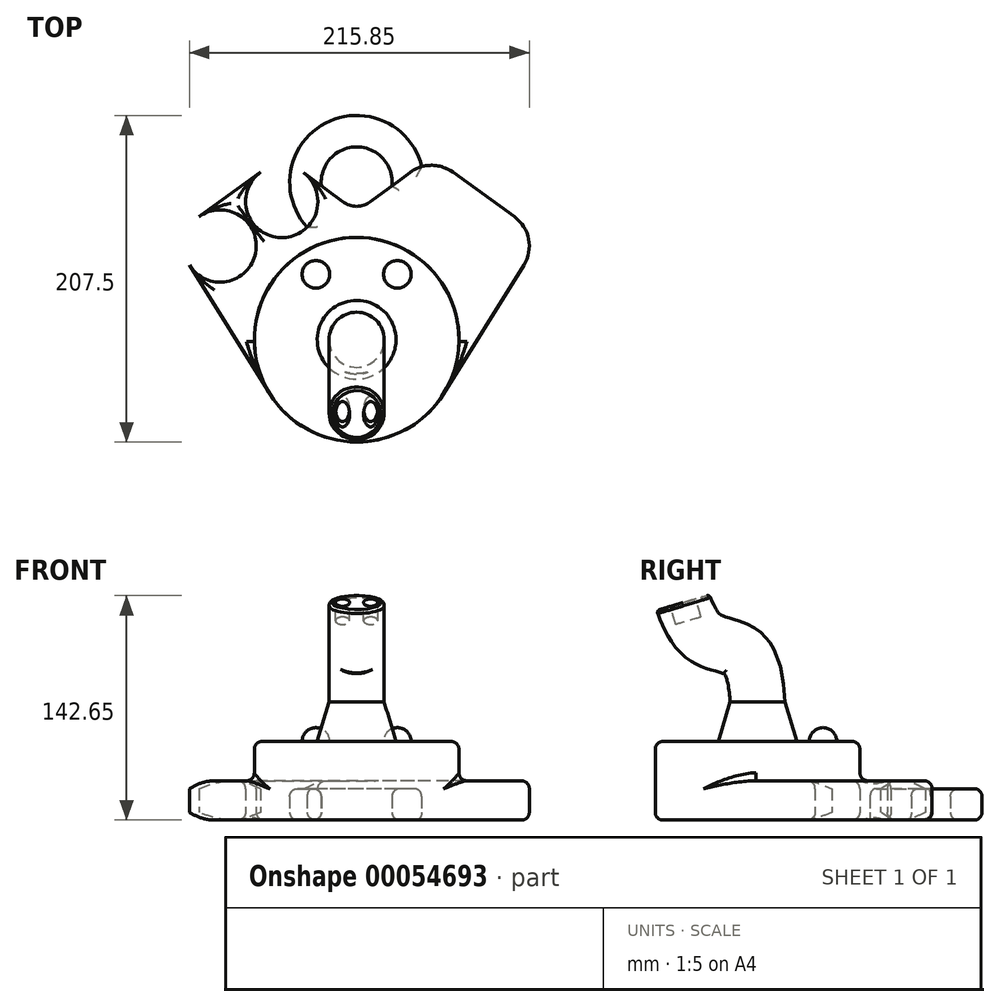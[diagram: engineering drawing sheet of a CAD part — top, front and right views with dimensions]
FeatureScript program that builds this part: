
annotation { "Feature Type Name" : "Feature", "Feature Type Description" : "" }
export const myFeature = defineFeature(function(context is Context, id is Id, definition is map)
    precondition{}
    {
        {
            var Q0;
            Q0=qCreatedBy(makeId("Top.planeOp"),FACE);
            var sketch = newSketch(context, id + "F0", { "sketchPlane" : qUnion([Q0])});
            skCircle(sketch, "E0", {"center": v(0, 0) * mm, "radius": 65 * mm});
            skSolve(sketch);
        }
        {
            var Q0;
            Q0=makeQuery(id+"F0.imprint","IMPRINT",FACE,{"disambiguationData":[TD([[makeQuery(id+"F0.imprint","IMPRINT",EDGE,{"derivedFrom":sQuery(id+"F0.wireOp",EDGE,"E0")}),1.0]])]});
            extrude(context, id + "F1", {"entities" : qUnion([Q0]), "depth" : 50 * mm});
        }
        {
            var Q0;
            Q0=makeQuery(id+"F1.opExtrude","CAP_EDGE",EDGE,{"disambiguationData":[OSD([sQuery(id+"F0.wireOp",EDGE,"E0")])],"isStart":false});
            fillet(context, id + "F2", {"entities" : qUnion([Q0]), "radius" : 5 * mm, "tangentPropagation" : true, "allowEdgeOverflow" : false});
        }
        {
            var Q0;
            Q0=makeQuery(id+"F1.opExtrude","CAP_FACE",FACE,{"disambiguationData":[OSD([sQuery(id+"F0.wireOp",EDGE,"E0")])],"isStart":false});
            var sketch = newSketch(context, id + "F3", { "sketchPlane" : qUnion([Q0])});
            skCircle(sketch, "E1", {"center": v(0, 0) * mm, "radius": 25 * mm});
            skSolve(sketch);
        }
        {
            var Q0;
            Q0=qCreatedBy(makeId("Right.planeOp"),FACE);
            var sketch = newSketch(context, id + "F4", { "sketchPlane" : qUnion([Q0])});
            skLineSegment(sketch, "E2.0", {"start": v(-25, 50) * mm, "end": v(25, 50) * mm});
            skPoint(sketch, "E3", {"position": v(0, 50) * mm});
            skLineSegment(sketch, "E4", {"start": v(0, 50) * mm, "end": v(0, 75) * mm, "construction": true});
            skSolve(sketch);
        }
        {
            var Q0;
            Q0=qCreatedBy(makeId("Top.planeOp"),FACE);
            var sketch = newSketch(context, id + "F5", { "sketchPlane" : qUnion([Q0])});
            skCircle(sketch, "E5", {"center": v(47.58, 87.83) * mm, "radius": 22.96 * mm});
            skCircle(sketch, "E6", {"center": v(86.7, 59.5) * mm, "radius": 22.96 * mm});
            skCircle(sketch, "E7.0", {"center": v(0, 0) * mm, "radius": 65 * mm});
            skLineSegment(sketch, "E8", {"start": v(106.18, 47.35) * mm, "end": v(55.14, -34.42) * mm});
            skLineSegment(sketch, "E9", {"start": v(33.87, 106.25) * mm, "end": v(-38.81, 52.14) * mm});
            skLineSegment(sketch, "E10", {"start": v(100.17, 78.1) * mm, "end": v(61.05, 106.43) * mm});
            skLineSegment(sketch, "E11", {"start": v(0, 36.31) * mm, "end": v(0, -43.27) * mm, "construction": true});
            skLineSegment(sketch, "E12.MirrorCS", {"start": v(-33.87, 106.25) * mm, "end": v(38.81, 52.14) * mm});
            skCircle(sketch, "E13.MirrorC", {"center": v(-47.58, 87.83) * mm, "radius": 22.96 * mm});
            skLineSegment(sketch, "E14.MirrorCS", {"start": v(-106.18, 47.35) * mm, "end": v(-55.14, -34.42) * mm});
            skLineSegment(sketch, "E15.MirrorCS", {"start": v(-100.17, 78.1) * mm, "end": v(-61.05, 106.43) * mm});
            skCircle(sketch, "E16.MirrorC", {"center": v(-86.7, 59.5) * mm, "radius": 22.96 * mm});
            skSolve(sketch);
        }
        {
            var Q0;
            {var subQ9=sQuery(id+"F5.wireOp",EDGE,"E14.MirrorCS");Q0=makeQuery(id+"F5.imprint","IMPRINT",FACE,{"disambiguationData":[TD([[makeQuery(id+"F5.imprint","IMPRINT",EDGE,{"derivedFrom":subQ9}),1.0]])]});}
            var Q1;
            {var subQ0=sQuery(id+"F5.wireOp",EDGE,"E16.MirrorC");var subQ1=makeQuery(id+"F5.imprint","INTERSECT",VERTEX,{"derivedFrom":[sQuery(id+"F5.wireOp",EDGE,"E14.MirrorCS"),subQ0]});Q1=makeQuery(id+"F5.imprint","IMPRINT",FACE,{"disambiguationData":[TD([[makeQuery(id+"F5.imprint","IMPRINT",EDGE,{"disambiguationData":[TD([[subQ1,1.0]])],"derivedFrom":subQ0}),-1.0]])]});}
            var Q2;
            {var subQ0=sQuery(id+"F5.wireOp",EDGE,"E13.MirrorC");var subQ1=makeQuery(id+"F5.imprint","INTERSECT",VERTEX,{"derivedFrom":[sQuery(id+"F5.wireOp",EDGE,"E12.MirrorCS"),subQ0]});Q2=makeQuery(id+"F5.imprint","IMPRINT",FACE,{"disambiguationData":[TD([[makeQuery(id+"F5.imprint","IMPRINT",EDGE,{"disambiguationData":[TD([[subQ1,1.0]])],"derivedFrom":subQ0}),-1.0]])]});}
            var Q3;
            {var subQ0=sQuery(id+"F5.wireOp",EDGE,"E8");Q3=makeQuery(id+"F5.imprint","IMPRINT",FACE,{"disambiguationData":[TD([[makeQuery(id+"F5.imprint","IMPRINT",EDGE,{"derivedFrom":subQ0}),-1.0]])]});}
            var Q4;
            {var subQ0=sQuery(id+"F5.wireOp",EDGE,"E5");var subQ1=makeQuery(id+"F5.imprint","INTERSECT",VERTEX,{"derivedFrom":[subQ0,sQuery(id+"F5.wireOp",EDGE,"E9")]});Q4=makeQuery(id+"F5.imprint","IMPRINT",FACE,{"disambiguationData":[TD([[makeQuery(id+"F5.imprint","IMPRINT",EDGE,{"disambiguationData":[TD([[subQ1,1.0]])],"derivedFrom":subQ0}),1.0]])]});}
            var Q5;
            {var subQ0=sQuery(id+"F5.wireOp",EDGE,"E6");var subQ1=makeQuery(id+"F5.imprint","INTERSECT",VERTEX,{"derivedFrom":[subQ0,sQuery(id+"F5.wireOp",EDGE,"E8")]});Q5=makeQuery(id+"F5.imprint","IMPRINT",FACE,{"disambiguationData":[TD([[makeQuery(id+"F5.imprint","IMPRINT",EDGE,{"disambiguationData":[TD([[subQ1,1.0]])],"derivedFrom":subQ0}),1.0]])]});}
            var Q6;
            {var subQ0=sQuery(id+"F5.wireOp",EDGE,"E9");var subQ1=sQuery(id+"F5.wireOp",EDGE,"E7.0");var subQ2=makeQuery(id+"F5.imprint","INTERSECT",VERTEX,{"derivedFrom":[subQ1,subQ0]});Q6=makeQuery(id+"F5.imprint","IMPRINT",FACE,{"disambiguationData":[TD([[makeQuery(id+"F5.imprint","IMPRINT",EDGE,{"disambiguationData":[TD([[subQ2,1.0]])],"derivedFrom":subQ1}),-1.0]])]});}
            extrude(context, id + "F6", {"entities" : qUnion([Q0, Q1, Q2, Q3, Q4, Q5, Q6]), "operationType" : NewBodyOperationType.ADD, "depth" : 25 * mm});
        }
        {
            var Q0;
            Q0=makeQuery(id+"F6.opExtrude","SWEPT_EDGE",EDGE,{"disambiguationData":[OSD([sQuery(id+"F5.wireOp",EDGE,"E9"),sQuery(id+"F5.wireOp",EDGE,"E12.MirrorCS")])]});
            fillet(context, id + "F7", {"entities" : qUnion([Q0]), "radius" : 15 * mm, "tangentPropagation" : true, "allowEdgeOverflow" : false});
        }
        {
            var Q0;
            Q0=makeQuery(id+"F1.opExtrude","CAP_FACE",FACE,{"disambiguationData":[OSD([sQuery(id+"F0.wireOp",EDGE,"E0")])],"isStart":false});
            var sketch = newSketch(context, id + "F8", { "sketchPlane" : qUnion([Q0])});
            skCircle(sketch, "E17", {"center": v(-25.88, 41.53) * mm, "radius": 8.75 * mm});
            skLineSegment(sketch, "E18", {"start": v(0, 69.37) * mm, "end": v(0, -46.75) * mm, "construction": true});
            skCircle(sketch, "E19.MirrorC", {"center": v(25.88, 41.53) * mm, "radius": 8.75 * mm});
            skLineSegment(sketch, "E20", {"start": v(-25.88, 50.28) * mm, "end": v(-25.88, 32.78) * mm});
            skLineSegment(sketch, "E21", {"start": v(25.88, 50.28) * mm, "end": v(25.88, 32.78) * mm});
            skSolve(sketch);
        }
        {
            var Q0;
            {var subQ0=sQuery(id+"F8.wireOp",EDGE,"E20");Q0=makeQuery(id+"F8.imprint","IMPRINT",FACE,{"disambiguationData":[TD([[makeQuery(id+"F8.imprint","IMPRINT",EDGE,{"derivedFrom":subQ0}),1.0]])]});}
            var Q1;
            Q1=sQuery(id+"F8.wireOp",EDGE,"E20");
            revolve(context, id + "F9", {"operationType" : NewBodyOperationType.ADD, "entities" : qUnion([Q0]), "axis" : qUnion([Q1]), "revolveType" : RevolveType.FULL});
        }
        {
            var Q0;
            {var subQ0=sQuery(id+"F8.wireOp",EDGE,"E21");Q0=makeQuery(id+"F8.imprint","IMPRINT",FACE,{"disambiguationData":[TD([[makeQuery(id+"F8.imprint","IMPRINT",EDGE,{"derivedFrom":subQ0}),1.0]])]});}
            var Q1;
            Q1=sQuery(id+"F8.wireOp",EDGE,"E21");
            revolve(context, id + "F10", {"operationType" : NewBodyOperationType.ADD, "entities" : qUnion([Q0]), "axis" : qUnion([Q1]), "revolveType" : RevolveType.FULL});
        }
        {
            var Q0;
            Q0=qCreatedBy(makeId("Top.planeOp"),FACE);
            cPlane(context, id + "F11", {"entities" : qUnion([Q0]), "cplaneType" : CPlaneType.OFFSET, "offset" : 75 * mm, "width" : 150 * mm, "height" : 150 * mm});
        }
        {
            var Q0;
            Q0=qCreatedBy(id+"F11.planeOp",FACE);
            var sketch = newSketch(context, id + "F12", { "sketchPlane" : qUnion([Q0])});
            skPoint(sketch, "E22.0", {"position": v(0, 0) * mm});
            skCircle(sketch, "E23", {"center": v(0, 0) * mm, "radius": 17.5 * mm});
            skSolve(sketch);
        }
        {
            var Q0;
            Q0=qCreatedBy(makeId("Right.planeOp"),FACE);
            var sketch = newSketch(context, id + "F13", { "sketchPlane" : qUnion([Q0])});
            skPoint(sketch, "E24.0", {"position": v(0, 75) * mm});
            skFitSpline(sketch, "E25", {"points": [v(0, 75) * mm, v(-9.9, 106.24) * mm, v(-32, 115.17) * mm, v(-47.33, 138.15) * mm], "startDerivative": vector(-6.33, 114.54) * mm, "endDerivative": vector(-32.6, 91.73) * mm});
            skSolve(sketch);
        }
        {
            var Q0;
            Q0=makeQuery(id+"F12.imprint","IMPRINT",FACE,{"disambiguationData":[TD([[makeQuery(id+"F12.imprint","IMPRINT",EDGE,{"derivedFrom":sQuery(id+"F12.wireOp",EDGE,"E23")}),1.0]])]});
            var Q1;
            Q1=sQuery(id+"F13.wireOp",EDGE,"E25");
            sweep(context, id + "F14", {"operationType" : NewBodyOperationType.ADD, "profiles" : qUnion([Q0]), "path" : qUnion([Q1])});
        }
        {
            var Q0;
            Q0=makeQuery(id+"F3.imprint","IMPRINT",FACE,{"disambiguationData":[TD([[makeQuery(id+"F3.imprint","IMPRINT",EDGE,{"derivedFrom":sQuery(id+"F3.wireOp",EDGE,"E1")}),1.0]])]});
            var Q1;
            Q1=makeQuery(id+"F12.imprint","IMPRINT",FACE,{"disambiguationData":[TD([[makeQuery(id+"F12.imprint","IMPRINT",EDGE,{"derivedFrom":sQuery(id+"F12.wireOp",EDGE,"E23")}),1.0]])]});
            loft(context, id + "F15", {"operationType" : NewBodyOperationType.ADD, "sheetProfilesArray" : [{ "sheetProfileEntities" : qUnion([Q0]) }, { "sheetProfileEntities" : qUnion([Q1]) }]});
        }
        {
            var Q0;
            Q0=makeQuery(id+"F14.opSweep","CAP_FACE",FACE,{"disambiguationData":[OSD([sQuery(id+"F12.wireOp",EDGE,"E23"),sQuery(id+"F13.wireOp",VERTEX,"E25.end")])],"isStart":false});
            var sketch = newSketch(context, id + "F16", { "sketchPlane" : qUnion([Q0])});
            skLineSegment(sketch, "E26.0", {"start": v(0, 80.66) * mm, "end": v(0, -30.73) * mm, "construction": true});
            skLineSegment(sketch, "E27", {"start": v(0, -23.9) * mm, "end": v(0, 11.1) * mm});
            skPoint(sketch, "E28", {"position": v(0, -6.4) * mm});
            skEllipse(sketch, "E29", {"center": v(-8.93, -6.4) * mm, "majorRadius": 8.4 * mm, "minorRadius": 4.5 * mm, "majorAxis": v(0, 1)});
            skEllipse(sketch, "E30.MirrorC", {"center": v(8.93, -6.4) * mm, "majorRadius": 8.4 * mm, "minorRadius": 4.5 * mm, "majorAxis": v(0, 1)});
            skSolve(sketch);
        }
        {
            var Q0;
            Q0=qCreatedBy(makeId("Top.planeOp"),FACE);
            var sketch = newSketch(context, id + "F17", { "sketchPlane" : qUnion([Q0])});
            skLineSegment(sketch, "E31", {"start": v(0, -116.18) * mm, "end": v(0, 155.02) * mm, "construction": true});
            skPoint(sketch, "E32", {"position": v(0, 100) * mm});
            skCircle(sketch, "E33", {"center": v(0, 100) * mm, "radius": 22.5 * mm});
            skCircle(sketch, "E34", {"center": v(0, 100) * mm, "radius": 42.5 * mm});
            skSolve(sketch);
        }
        {
            var Q0;
            Q0=makeQuery(id+"F16.imprint","IMPRINT",FACE,{"disambiguationData":[TD([[makeQuery(id+"F16.imprint","IMPRINT",EDGE,{"derivedFrom":sQuery(id+"F16.wireOp",EDGE,"E29")}),1.0]])]});
            var Q1;
            Q1=makeQuery(id+"F16.imprint","IMPRINT",FACE,{"disambiguationData":[TD([[makeQuery(id+"F16.imprint","IMPRINT",EDGE,{"derivedFrom":sQuery(id+"F16.wireOp",EDGE,"E30.MirrorC")}),1.0]])]});
            var Q2;
            Q2=sQuery(id+"F16.wireOp",EDGE,"E30.MirrorC");
            var Q3;
            Q3=sQuery(id+"F16.wireOp",EDGE,"E29");
            extrude(context, id + "F18", {"entities" : qUnion([Q0, Q1]), "operationType" : NewBodyOperationType.REMOVE, "surfaceEntities" : qUnion([Q2, Q3]), "oppositeDirection" : true, "depth" : 12 * mm});
        }
        {
            var Q0;
            Q0=makeQuery(id+"F17.imprint","IMPRINT",FACE,{"disambiguationData":[TD([[makeQuery(id+"F17.imprint","IMPRINT",EDGE,{"derivedFrom":sQuery(id+"F17.wireOp",EDGE,"E33")}),-1.0]])]});
            extrude(context, id + "F19", {"entities" : qUnion([Q0]), "operationType" : NewBodyOperationType.ADD, "depth" : 20 * mm});
        }
        {
            var Q0;
            Q0=makeQuery(id+"F19.opExtrude","CAP_EDGE",EDGE,{"disambiguationData":[OSD([sQuery(id+"F17.wireOp",EDGE,"E33")])],"isStart":false});
            var Q1;
            Q1=makeQuery(id+"F19.opExtrude","CAP_EDGE",EDGE,{"disambiguationData":[OSD([sQuery(id+"F17.wireOp",EDGE,"E34")])],"isStart":false});
            fillet(context, id + "F20", {"entities" : qUnion([Q0, Q1]), "radius" : 5 * mm, "tangentPropagation" : true, "allowEdgeOverflow" : false});
        }
        {
            var Q0;
            Q0=makeQuery(id+"F6.opExtrude","CAP_FACE",FACE,{"disambiguationData":[OSD([sQuery(id+"F5.wireOp",EDGE,"E5"),sQuery(id+"F5.wireOp",EDGE,"E6"),sQuery(id+"F5.wireOp",EDGE,"E7.0"),sQuery(id+"F5.wireOp",EDGE,"E8"),sQuery(id+"F5.wireOp",EDGE,"E9"),sQuery(id+"F5.wireOp",EDGE,"E10"),sQuery(id+"F5.wireOp",EDGE,"E12.MirrorCS"),sQuery(id+"F5.wireOp",EDGE,"E13.MirrorC"),sQuery(id+"F5.wireOp",EDGE,"E14.MirrorCS"),sQuery(id+"F5.wireOp",EDGE,"E15.MirrorCS"),sQuery(id+"F5.wireOp",EDGE,"E16.MirrorC")])],"isStart":false});
            fillet(context, id + "F21", {"entities" : qUnion([Q0]), "radius" : 5 * mm, "tangentPropagation" : true, "allowEdgeOverflow" : false});
        }
        {
            var Q0;
            Q0=makeQuery(id+"F19.boolean.opBoolean","MERGE",FACE,{"derivedFrom":[makeQuery(id+"F6.boolean.opBoolean","MERGE",FACE,{"derivedFrom":[makeQuery(id+"F1.opExtrude","CAP_FACE",FACE,{"disambiguationData":[OSD([sQuery(id+"F0.wireOp",EDGE,"E0")])],"isStart":true}),makeQuery(id+"F6.opExtrude","CAP_FACE",FACE,{"disambiguationData":[OSD([sQuery(id+"F5.wireOp",EDGE,"E5"),sQuery(id+"F5.wireOp",EDGE,"E6"),sQuery(id+"F5.wireOp",EDGE,"E7.0"),sQuery(id+"F5.wireOp",EDGE,"E8"),sQuery(id+"F5.wireOp",EDGE,"E9"),sQuery(id+"F5.wireOp",EDGE,"E10"),sQuery(id+"F5.wireOp",EDGE,"E12.MirrorCS"),sQuery(id+"F5.wireOp",EDGE,"E13.MirrorC"),sQuery(id+"F5.wireOp",EDGE,"E14.MirrorCS"),sQuery(id+"F5.wireOp",EDGE,"E15.MirrorCS"),sQuery(id+"F5.wireOp",EDGE,"E16.MirrorC")])],"isStart":true})]}),makeQuery(id+"F19.opExtrude","CAP_FACE",FACE,{"disambiguationData":[OSD([sQuery(id+"F17.wireOp",EDGE,"E33"),sQuery(id+"F17.wireOp",EDGE,"E34")])],"isStart":true})]});
            fillet(context, id + "F22", {"entities" : qUnion([Q0]), "radius" : 5 * mm, "tangentPropagation" : true, "allowEdgeOverflow" : false});
        }
        {
            var Q0;
            Q0=makeQuery(id+"F14.opSweep","CAP_EDGE",EDGE,{"disambiguationData":[OSD([sQuery(id+"F12.wireOp",EDGE,"E23"),sQuery(id+"F13.wireOp",VERTEX,"E25.end")])],"isStart":false});
            fillet(context, id + "F23", {"entities" : qUnion([Q0]), "radius" : 2 * mm, "tangentPropagation" : true, "allowEdgeOverflow" : false});
        }
    });
